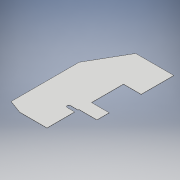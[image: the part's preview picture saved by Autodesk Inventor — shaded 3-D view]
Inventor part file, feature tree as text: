
AUTODESK INVENTOR PART (.ipt)
format: ipt  version: 2018 (Build 220112000, 112)  size: 118,272 bytes
history: native  units: mm
features: extrude x1, sketch x1
ambient origin geometry x8: Origin, YZ Plane, XZ Plane, XY Plane, X Axis, Y Axis, Z Axis, Center Point
bodies: Solid1 (feature_tree)
feature tree (2):
  extrude  "Extrusion1"  Depth=25.0mm
  sketch  "Sketch1"  dims[d0=200.0mm d1=27.925268mm d2=500.0mm d3=100.0mm d4=60.0deg d5=280.0mm d6=800.0mm d7=240.0mm d8=130.0mm d9=235.0mm d10=130.0mm d11=235.0mm d12=1.6mm d13=0.0mm d14=25.0mm d16=216.0mm d17=0.0mm d18=55.0mm]
